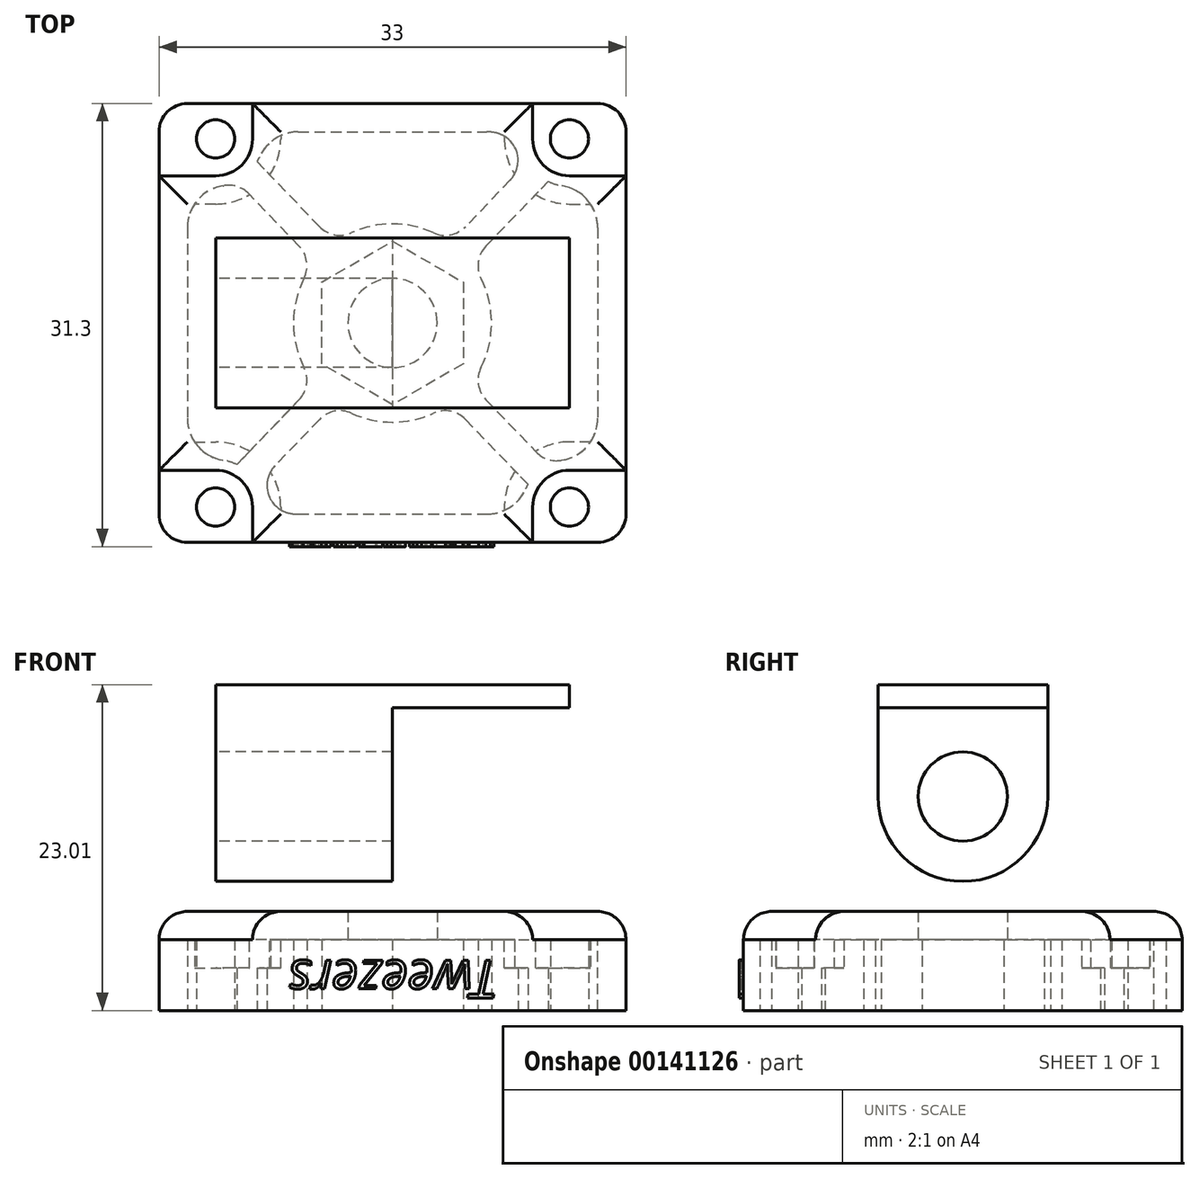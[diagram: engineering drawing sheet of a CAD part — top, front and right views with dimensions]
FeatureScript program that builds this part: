
annotation { "Feature Type Name" : "Feature", "Feature Type Description" : "" }
export const myFeature = defineFeature(function(context is Context, id is Id, definition is map)
    precondition{}
    {
        {
            var Q0;
            Q0=qCreatedBy(makeId("Top.planeOp"),FACE);
            var sketch = newSketch(context, id + "F0", { "sketchPlane" : qUnion([Q0])});
            skPoint(sketch, "E0", {"position": v(-12.5, 13) * mm});
            skPoint(sketch, "E1", {"position": v(12.5, 13) * mm});
            skPoint(sketch, "E2", {"position": v(-12.5, -13) * mm});
            skPoint(sketch, "E3", {"position": v(12.5, -13) * mm});
            skLineSegment(sketch, "E4", {"start": v(0, 33.85) * mm, "end": v(0, -36.04) * mm, "construction": true});
            skLineSegment(sketch, "E5", {"start": v(-33.7, 0) * mm, "end": v(36.4, 0) * mm, "construction": true});
            skLineSegment(sketch, "E6.bottom", {"start": v(-16.5, 15.5) * mm, "end": v(16.5, 15.5) * mm});
            skLineSegment(sketch, "E6.top", {"start": v(-16.5, -15.5) * mm, "end": v(16.5, -15.5) * mm});
            skLineSegment(sketch, "E6.left", {"start": v(-16.5, 15.5) * mm, "end": v(-16.5, -15.5) * mm});
            skLineSegment(sketch, "E6.right", {"start": v(16.5, 15.5) * mm, "end": v(16.5, -15.5) * mm});
            skCircle(sketch, "E7", {"center": v(-12.5, 13) * mm, "radius": 1.35 * mm});
            skCircle(sketch, "E8", {"center": v(12.5, 13) * mm, "radius": 1.35 * mm});
            skCircle(sketch, "E9", {"center": v(-12.5, -13) * mm, "radius": 1.35 * mm});
            skCircle(sketch, "E10", {"center": v(12.5, -13) * mm, "radius": 1.35 * mm});
            skSolve(sketch);
        }
        {
            var Q0;
            Q0=makeQuery(id+"F0.imprint","IMPRINT",FACE,{"disambiguationData":[TD([[makeQuery(id+"F0.imprint","IMPRINT",EDGE,{"derivedFrom":sQuery(id+"F0.wireOp",EDGE,"E6.bottom")}),-1.0]])]});
            extrude(context, id + "F1", {"entities" : qUnion([Q0]), "depth" : 7 * mm});
        }
        {
            var Q0;
            Q0=makeQuery(id+"F1.opExtrude","CAP_FACE",FACE,{"disambiguationData":[OSD([sQuery(id+"F0.wireOp",EDGE,"E6.bottom"),sQuery(id+"F0.wireOp",EDGE,"E6.top"),sQuery(id+"F0.wireOp",EDGE,"E6.left"),sQuery(id+"F0.wireOp",EDGE,"E6.right"),sQuery(id+"F0.wireOp",EDGE,"E7"),sQuery(id+"F0.wireOp",EDGE,"E8"),sQuery(id+"F0.wireOp",EDGE,"E9"),sQuery(id+"F0.wireOp",EDGE,"E10")])],"isStart":false});
            var sketch = newSketch(context, id + "F2", { "sketchPlane" : qUnion([Q0])});
            skLineSegment(sketch, "E11", {"start": v(9.9, 15.5) * mm, "end": v(9.9, 13) * mm});
            skLineSegment(sketch, "E12", {"start": v(12.5, 10.4) * mm, "end": v(16.5, 10.4) * mm});
            skPoint(sketch, "E13.visualSharp", {"position": v(9.9, 10.4) * mm});
            skArc(sketch, "E13.filletArc", {"start": v(9.9, 13) * mm, "mid": v(10.66, 11.16) * mm, "end": v(12.5, 10.4) * mm});
            skLineSegment(sketch, "E14", {"start": v(-9.9, 15.5) * mm, "end": v(-9.9, 13) * mm});
            skLineSegment(sketch, "E15", {"start": v(-12.5, 10.4) * mm, "end": v(-16.5, 10.4) * mm});
            skPoint(sketch, "E16.visualSharp", {"position": v(-9.9, 10.4) * mm});
            skArc(sketch, "E16.filletArc", {"start": v(-12.5, 10.4) * mm, "mid": v(-10.66, 11.16) * mm, "end": v(-9.9, 13) * mm});
            skLineSegment(sketch, "E17", {"start": v(-16.5, -10.4) * mm, "end": v(-12.5, -10.4) * mm});
            skLineSegment(sketch, "E18", {"start": v(-9.9, -13) * mm, "end": v(-9.9, -15.5) * mm});
            skPoint(sketch, "E19.visualSharp", {"position": v(-9.9, -10.4) * mm});
            skArc(sketch, "E19.filletArc", {"start": v(-9.9, -13) * mm, "mid": v(-10.66, -11.16) * mm, "end": v(-12.5, -10.4) * mm});
            skLineSegment(sketch, "E20", {"start": v(16.5, -10.4) * mm, "end": v(12.5, -10.4) * mm});
            skLineSegment(sketch, "E21", {"start": v(9.9, -13) * mm, "end": v(9.9, -15.5) * mm});
            skPoint(sketch, "E22.visualSharp", {"position": v(9.9, -10.4) * mm});
            skArc(sketch, "E22.filletArc", {"start": v(12.5, -10.4) * mm, "mid": v(10.66, -11.16) * mm, "end": v(9.9, -13) * mm});
            skSolve(sketch);
        }
        {
            var Q0;
            Q0=makeQuery(id+"F2.imprint","IMPRINT",FACE,{"disambiguationData":[TD([[makeQuery(id+"F2.imprint","IMPRINT",EDGE,{"derivedFrom":makeQuery(id+"F1.opExtrude","CAP_EDGE",EDGE,{"disambiguationData":[OSD([sQuery(id+"F0.wireOp",EDGE,"E7")])],"isStart":false})}),-1.0]])]});
            var Q1;
            Q1=makeQuery(id+"F2.imprint","IMPRINT",FACE,{"disambiguationData":[TD([[makeQuery(id+"F2.imprint","IMPRINT",EDGE,{"derivedFrom":makeQuery(id+"F1.opExtrude","CAP_EDGE",EDGE,{"disambiguationData":[OSD([sQuery(id+"F0.wireOp",EDGE,"E8")])],"isStart":false})}),-1.0]])]});
            var Q2;
            {var subQ4=sQuery(id+"F2.wireOp",EDGE,"E17");Q2=makeQuery(id+"F2.imprint","IMPRINT",FACE,{"disambiguationData":[TD([[makeQuery(id+"F2.imprint","IMPRINT",EDGE,{"derivedFrom":subQ4}),-1.0]])]});}
            var Q3;
            {var subQ1=sQuery(id+"F2.wireOp",EDGE,"E20");Q3=makeQuery(id+"F2.imprint","IMPRINT",FACE,{"disambiguationData":[TD([[makeQuery(id+"F2.imprint","IMPRINT",EDGE,{"derivedFrom":subQ1}),1.0]])]});}
            extrude(context, id + "F3", {"entities" : qUnion([Q0, Q1, Q2, Q3]), "operationType" : NewBodyOperationType.REMOVE, "oppositeDirection" : true, "depth" : 2 * mm});
        }
        {
            var Q0;
            Q0=makeQuery(id+"F1.opExtrude","CAP_FACE",FACE,{"disambiguationData":[OSD([sQuery(id+"F0.wireOp",EDGE,"E6.bottom"),sQuery(id+"F0.wireOp",EDGE,"E6.top"),sQuery(id+"F0.wireOp",EDGE,"E6.left"),sQuery(id+"F0.wireOp",EDGE,"E6.right"),sQuery(id+"F0.wireOp",EDGE,"E7"),sQuery(id+"F0.wireOp",EDGE,"E8"),sQuery(id+"F0.wireOp",EDGE,"E9"),sQuery(id+"F0.wireOp",EDGE,"E10")])],"isStart":true});
            shell(context, id + "F4", {"entities" : qUnion([Q0]), "thickness" : 2 * mm});
        }
        {
            var Q0;
            Q0=makeQuery(id+"F1.opExtrude","CAP_FACE",FACE,{"disambiguationData":[OSD([sQuery(id+"F0.wireOp",EDGE,"E6.bottom"),sQuery(id+"F0.wireOp",EDGE,"E6.top"),sQuery(id+"F0.wireOp",EDGE,"E6.left"),sQuery(id+"F0.wireOp",EDGE,"E6.right"),sQuery(id+"F0.wireOp",EDGE,"E7"),sQuery(id+"F0.wireOp",EDGE,"E8"),sQuery(id+"F0.wireOp",EDGE,"E9"),sQuery(id+"F0.wireOp",EDGE,"E10")])],"isStart":false});
            var Q1;
            Q1=makeQuery(id+"F3.boolean.opBoolean","COPY",EDGE,{"derivedFrom":makeQuery(id+"F3.opExtrude","SWEPT_EDGE",EDGE,{"disambiguationData":[OSD([sQuery(id+"F0.wireOp",EDGE,"E6.top"),sQuery(id+"F2.wireOp",EDGE,"E18")])]})});
            var Q2;
            Q2=makeQuery(id+"F3.boolean.opBoolean","COPY",EDGE,{"derivedFrom":makeQuery(id+"F3.opExtrude","SWEPT_EDGE",EDGE,{"disambiguationData":[OSD([sQuery(id+"F0.wireOp",EDGE,"E6.left"),sQuery(id+"F2.wireOp",EDGE,"E17")])]})});
            var Q3;
            Q3=makeQuery(id+"F1.opExtrude","SWEPT_EDGE",EDGE,{"disambiguationData":[OSD([sQuery(id+"F0.wireOp",EDGE,"E6.bottom"),sQuery(id+"F0.wireOp",EDGE,"E6.right")])]});
            var Q4;
            Q4=makeQuery(id+"F3.boolean.opBoolean","COPY",EDGE,{"derivedFrom":makeQuery(id+"F3.opExtrude","SWEPT_EDGE",EDGE,{"disambiguationData":[OSD([sQuery(id+"F0.wireOp",EDGE,"E6.bottom"),sQuery(id+"F2.wireOp",EDGE,"E11")])]})});
            var Q5;
            Q5=makeQuery(id+"F3.boolean.opBoolean","COPY",EDGE,{"derivedFrom":makeQuery(id+"F3.opExtrude","SWEPT_EDGE",EDGE,{"disambiguationData":[OSD([sQuery(id+"F0.wireOp",EDGE,"E6.right"),sQuery(id+"F2.wireOp",EDGE,"E12")])]})});
            var Q6;
            Q6=makeQuery(id+"F3.boolean.opBoolean","COPY",EDGE,{"derivedFrom":makeQuery(id+"F3.opExtrude","SWEPT_EDGE",EDGE,{"disambiguationData":[OSD([sQuery(id+"F0.wireOp",EDGE,"E6.right"),sQuery(id+"F2.wireOp",EDGE,"E20")])]})});
            var Q7;
            Q7=makeQuery(id+"F1.opExtrude","SWEPT_EDGE",EDGE,{"disambiguationData":[OSD([sQuery(id+"F0.wireOp",EDGE,"E6.top"),sQuery(id+"F0.wireOp",EDGE,"E6.right")])]});
            var Q8;
            Q8=makeQuery(id+"F3.boolean.opBoolean","COPY",EDGE,{"derivedFrom":makeQuery(id+"F3.opExtrude","SWEPT_EDGE",EDGE,{"disambiguationData":[OSD([sQuery(id+"F0.wireOp",EDGE,"E6.top"),sQuery(id+"F2.wireOp",EDGE,"E21")])]})});
            var Q9;
            Q9=makeQuery(id+"F1.opExtrude","SWEPT_EDGE",EDGE,{"disambiguationData":[OSD([sQuery(id+"F0.wireOp",EDGE,"E6.top"),sQuery(id+"F0.wireOp",EDGE,"E6.left")])]});
            var Q10;
            Q10=makeQuery(id+"F3.boolean.opBoolean","COPY",EDGE,{"derivedFrom":makeQuery(id+"F3.opExtrude","SWEPT_EDGE",EDGE,{"disambiguationData":[OSD([sQuery(id+"F0.wireOp",EDGE,"E6.left"),sQuery(id+"F2.wireOp",EDGE,"E15")])]})});
            var Q11;
            Q11=makeQuery(id+"F3.boolean.opBoolean","COPY",EDGE,{"derivedFrom":makeQuery(id+"F3.opExtrude","SWEPT_EDGE",EDGE,{"disambiguationData":[OSD([sQuery(id+"F0.wireOp",EDGE,"E6.bottom"),sQuery(id+"F2.wireOp",EDGE,"E14")])]})});
            var Q12;
            Q12=makeQuery(id+"F1.opExtrude","SWEPT_EDGE",EDGE,{"disambiguationData":[OSD([sQuery(id+"F0.wireOp",EDGE,"E6.bottom"),sQuery(id+"F0.wireOp",EDGE,"E6.left")])]});
            fillet(context, id + "F5", {"entities" : qUnion([Q0, Q1, Q2, Q3, Q4, Q5, Q6, Q7, Q8, Q9, Q10, Q11, Q12]), "radius" : 2 * mm, "tangentPropagation" : true, "allowEdgeOverflow" : false});
        }
        {
            var Q0;
            Q0=qCreatedBy(makeId("Top.planeOp"),FACE);
            var sketch = newSketch(context, id + "F6", { "sketchPlane" : qUnion([Q0])});
            skPoint(sketch, "E23", {"position": v(0, 0) * mm});
            skCircle(sketch, "E24", {"center": v(0, 0) * mm, "radius": 3.15 * mm});
            skCircle(sketch, "E25.cCircle", {"center": v(0, 0) * mm, "radius": 5 * mm, "construction": true});
            skLineSegment(sketch, "E25.0", {"start": v(5, 2.89) * mm, "end": v(5, -2.89) * mm});
            skLineSegment(sketch, "E25.1", {"start": v(5, -2.89) * mm, "end": v(0, -5.77) * mm});
            skLineSegment(sketch, "E25.2", {"start": v(0, -5.77) * mm, "end": v(-5, -2.89) * mm});
            skLineSegment(sketch, "E25.3", {"start": v(-5, -2.89) * mm, "end": v(-5, 2.89) * mm});
            skLineSegment(sketch, "E25.4", {"start": v(-5, 2.89) * mm, "end": v(0, 5.77) * mm});
            skLineSegment(sketch, "E25.5", {"start": v(0, 5.77) * mm, "end": v(5, 2.89) * mm});
            skPoint(sketch, "E25.0.midPoint", {"position": v(5, 0) * mm});
            skCircle(sketch, "E26", {"center": v(0, 0) * mm, "radius": 7 * mm});
            skLineSegment(sketch, "E27", {"start": v(-4.08, -5.69) * mm, "end": v(-9.56, -11.39) * mm});
            skLineSegment(sketch, "E28", {"start": v(-11, -10) * mm, "end": v(-5.52, -4.3) * mm});
            skLineSegment(sketch, "E29", {"start": v(-12.5, -13) * mm, "end": v(0, 0) * mm, "construction": true});
            skLineSegment(sketch, "E30", {"start": v(0, 0) * mm, "end": v(12.5, -13) * mm, "construction": true});
            skLineSegment(sketch, "E31", {"start": v(4.08, -5.69) * mm, "end": v(9.56, -11.39) * mm});
            skLineSegment(sketch, "E32", {"start": v(5.52, -4.3) * mm, "end": v(11, -10) * mm});
            skLineSegment(sketch, "E33", {"start": v(-4.08, 5.69) * mm, "end": v(-9.56, 11.39) * mm});
            skLineSegment(sketch, "E34", {"start": v(-5.52, 4.3) * mm, "end": v(-11, 10) * mm});
            skLineSegment(sketch, "E35", {"start": v(0, 0) * mm, "end": v(-12.5, 13) * mm, "construction": true});
            skLineSegment(sketch, "E36", {"start": v(12.5, 13) * mm, "end": v(0, 0) * mm, "construction": true});
            skArc(sketch, "E37.0", {"start": v(9.19, 13.5) * mm, "mid": v(10.78, 10.13) * mm, "end": v(14.5, 10.31) * mm});
            skLineSegment(sketch, "E38", {"start": v(5.52, 4.3) * mm, "end": v(11, 10) * mm});
            skLineSegment(sketch, "E39", {"start": v(9.56, 11.39) * mm, "end": v(4.08, 5.69) * mm});
            skArc(sketch, "E40.0", {"start": v(14.5, -10.31) * mm, "mid": v(10.78, -10.13) * mm, "end": v(9.19, -13.5) * mm});
            skArc(sketch, "E41.0", {"start": v(-9.19, -13.5) * mm, "mid": v(-10.78, -10.13) * mm, "end": v(-14.5, -10.31) * mm});
            skArc(sketch, "E42.0", {"start": v(-14.5, 10.31) * mm, "mid": v(-10.78, 10.13) * mm, "end": v(-9.19, 13.5) * mm});
            skSolve(sketch);
        }
        {
            var Q0;
            {var subQ0=sQuery(id+"F6.wireOp",EDGE,"E38");var subQ1=sQuery(id+"F6.wireOp",EDGE,"E26");var subQ2=makeQuery(id+"F6.imprint","INTERSECT",VERTEX,{"derivedFrom":[subQ1,subQ0]});Q0=makeQuery(id+"F6.imprint","IMPRINT",FACE,{"disambiguationData":[TD([[makeQuery(id+"F6.imprint","IMPRINT",EDGE,{"disambiguationData":[TD([[subQ2,-1.0]])],"derivedFrom":subQ1}),-1.0]])]});}
            var Q1;
            Q1=makeQuery(id+"F6.imprint","IMPRINT",FACE,{"disambiguationData":[TD([[makeQuery(id+"F6.imprint","IMPRINT",EDGE,{"derivedFrom":sQuery(id+"F6.wireOp",EDGE,"E25.0")}),1.0]])]});
            var Q2;
            {var subQ0=sQuery(id+"F6.wireOp",EDGE,"E27");Q2=makeQuery(id+"F6.imprint","IMPRINT",FACE,{"disambiguationData":[TD([[makeQuery(id+"F6.imprint","IMPRINT",EDGE,{"derivedFrom":subQ0}),-1.0]])]});}
            var Q3;
            {var subQ0=sQuery(id+"F6.wireOp",EDGE,"E33");Q3=makeQuery(id+"F6.imprint","IMPRINT",FACE,{"disambiguationData":[TD([[makeQuery(id+"F6.imprint","IMPRINT",EDGE,{"derivedFrom":subQ0}),1.0]])]});}
            var Q4;
            {var subQ0=sQuery(id+"F6.wireOp",EDGE,"E31");Q4=makeQuery(id+"F6.imprint","IMPRINT",FACE,{"disambiguationData":[TD([[makeQuery(id+"F6.imprint","IMPRINT",EDGE,{"derivedFrom":subQ0}),1.0]])]});}
            var Q5;
            Q5=makeQuery(id+"F4.opShell","OFFSET_FACE",FACE,{"disambiguationData":[OSD([sQuery(id+"F0.wireOp",EDGE,"E6.bottom"),sQuery(id+"F0.wireOp",EDGE,"E6.top"),sQuery(id+"F0.wireOp",EDGE,"E6.left"),sQuery(id+"F0.wireOp",EDGE,"E6.right"),sQuery(id+"F0.wireOp",EDGE,"E7"),sQuery(id+"F0.wireOp",EDGE,"E8"),sQuery(id+"F0.wireOp",EDGE,"E9"),sQuery(id+"F0.wireOp",EDGE,"E10")])]});
            extrude(context, id + "F7", {"entities" : qUnion([Q0, Q1, Q2, Q3, Q4]), "operationType" : NewBodyOperationType.ADD, "endBound" : BoundingType.UP_TO_SURFACE, "endBoundEntityFace" : qUnion([Q5]), "depth" : 25 * mm});
        }
        {
            var Q0;
            Q0=makeQuery(id+"F6.imprint","IMPRINT",FACE,{"disambiguationData":[TD([[makeQuery(id+"F6.imprint","IMPRINT",EDGE,{"derivedFrom":sQuery(id+"F6.wireOp",EDGE,"E24")}),1.0]])]});
            extrude(context, id + "F8", {"entities" : qUnion([Q0]), "operationType" : NewBodyOperationType.REMOVE, "endBound" : BoundingType.THROUGH_ALL, "depth" : 25 * mm});
        }
        {
            var Q0;
            Q0=makeQuery(id+"F4.opShell","TWEAK_EDGE",EDGE,{"derivedFrom":[makeQuery(id+"F1.opExtrude","SWEPT_FACE",FACE,{"disambiguationData":[OSD([sQuery(id+"F0.wireOp",EDGE,"E6.right")])]}),makeQuery(id+"F1.opExtrude","SWEPT_FACE",FACE,{"disambiguationData":[OSD([sQuery(id+"F0.wireOp",EDGE,"E10")])]})]});
            var Q1;
            Q1=makeQuery(id+"F4.opShell","TWEAK_EDGE",EDGE,{"derivedFrom":[makeQuery(id+"F1.opExtrude","SWEPT_FACE",FACE,{"disambiguationData":[OSD([sQuery(id+"F0.wireOp",EDGE,"E6.top")])]}),makeQuery(id+"F1.opExtrude","SWEPT_FACE",FACE,{"disambiguationData":[OSD([sQuery(id+"F0.wireOp",EDGE,"E10")])]})]});
            var Q2;
            Q2=makeQuery(id+"F4.opShell","TWEAK_EDGE",EDGE,{"derivedFrom":[makeQuery(id+"F1.opExtrude","SWEPT_FACE",FACE,{"disambiguationData":[OSD([sQuery(id+"F0.wireOp",EDGE,"E6.top")])]}),makeQuery(id+"F1.opExtrude","SWEPT_FACE",FACE,{"disambiguationData":[OSD([sQuery(id+"F0.wireOp",EDGE,"E9")])]})]});
            var Q3;
            Q3=makeQuery(id+"F4.opShell","TWEAK_EDGE",EDGE,{"derivedFrom":[makeQuery(id+"F1.opExtrude","SWEPT_FACE",FACE,{"disambiguationData":[OSD([sQuery(id+"F0.wireOp",EDGE,"E6.left")])]}),makeQuery(id+"F1.opExtrude","SWEPT_FACE",FACE,{"disambiguationData":[OSD([sQuery(id+"F0.wireOp",EDGE,"E9")])]})]});
            var Q4;
            Q4=makeQuery(id+"F4.opShell","TWEAK_EDGE",EDGE,{"derivedFrom":[makeQuery(id+"F1.opExtrude","SWEPT_FACE",FACE,{"disambiguationData":[OSD([sQuery(id+"F0.wireOp",EDGE,"E6.left")])]}),makeQuery(id+"F1.opExtrude","SWEPT_FACE",FACE,{"disambiguationData":[OSD([sQuery(id+"F0.wireOp",EDGE,"E7")])]})]});
            var Q5;
            Q5=makeQuery(id+"F4.opShell","TWEAK_EDGE",EDGE,{"derivedFrom":[makeQuery(id+"F1.opExtrude","SWEPT_FACE",FACE,{"disambiguationData":[OSD([sQuery(id+"F0.wireOp",EDGE,"E6.bottom")])]}),makeQuery(id+"F1.opExtrude","SWEPT_FACE",FACE,{"disambiguationData":[OSD([sQuery(id+"F0.wireOp",EDGE,"E7")])]})]});
            var Q6;
            Q6=makeQuery(id+"F4.opShell","TWEAK_EDGE",EDGE,{"derivedFrom":[makeQuery(id+"F1.opExtrude","SWEPT_FACE",FACE,{"disambiguationData":[OSD([sQuery(id+"F0.wireOp",EDGE,"E6.right")])]}),makeQuery(id+"F1.opExtrude","SWEPT_FACE",FACE,{"disambiguationData":[OSD([sQuery(id+"F0.wireOp",EDGE,"E8")])]})]});
            var Q7;
            Q7=makeQuery(id+"F4.opShell","TWEAK_EDGE",EDGE,{"derivedFrom":[makeQuery(id+"F1.opExtrude","SWEPT_FACE",FACE,{"disambiguationData":[OSD([sQuery(id+"F0.wireOp",EDGE,"E6.bottom")])]}),makeQuery(id+"F1.opExtrude","SWEPT_FACE",FACE,{"disambiguationData":[OSD([sQuery(id+"F0.wireOp",EDGE,"E8")])]})]});
            fillet(context, id + "F9", {"entities" : qUnion([Q0, Q1, Q2, Q3, Q4, Q5, Q6, Q7]), "radius" : 3 * mm, "allowEdgeOverflow" : false});
        }
        {
            var Q0;
            Q0=makeQuery(id+"F1.opExtrude","SWEPT_FACE",FACE,{"disambiguationData":[OSD([sQuery(id+"F0.wireOp",EDGE,"E6.top")])]});
            var sketch = newSketch(context, id + "F10", { "sketchPlane" : qUnion([Q0])});
            skText(sketch, "E43", { "text": "Tweezers", "fontName": "OpenSans-Italic.ttf"});
            const initialGuessF10  = {"E43": [0.0075, 0.00355, -1, 0, 0.0027]};
            skSetInitialGuess(sketch, initialGuessF10);
            skSolve(sketch);
        }
        {
            var Q0;
            Q0=qSketchRegion(id+"F10",true);
            extrude(context, id + "F11", {"entities" : qUnion([Q0]), "operationType" : NewBodyOperationType.ADD, "depth" : 0.3 * mm});
        }
        {
            var Q0;
            Q0=makeQuery(id+"F7.opExtrude","SWEPT_EDGE",EDGE,{"disambiguationData":[OSD([sQuery(id+"F6.wireOp",EDGE,"E26"),sQuery(id+"F6.wireOp",EDGE,"E28")])]});
            var Q1;
            Q1=makeQuery(id+"F7.opExtrude","SWEPT_EDGE",EDGE,{"disambiguationData":[OSD([sQuery(id+"F6.wireOp",EDGE,"E26"),sQuery(id+"F6.wireOp",EDGE,"E34")])]});
            var Q2;
            Q2=makeQuery(id+"F7.opExtrude","SWEPT_EDGE",EDGE,{"disambiguationData":[OSD([sQuery(id+"F6.wireOp",EDGE,"E26"),sQuery(id+"F6.wireOp",EDGE,"E33")])]});
            var Q3;
            Q3=makeQuery(id+"F7.opExtrude","SWEPT_EDGE",EDGE,{"disambiguationData":[OSD([sQuery(id+"F6.wireOp",EDGE,"E26"),sQuery(id+"F6.wireOp",EDGE,"E39")])]});
            var Q4;
            Q4=makeQuery(id+"F7.opExtrude","SWEPT_EDGE",EDGE,{"disambiguationData":[OSD([sQuery(id+"F6.wireOp",EDGE,"E26"),sQuery(id+"F6.wireOp",EDGE,"E38")])]});
            var Q5;
            Q5=makeQuery(id+"F7.opExtrude","SWEPT_EDGE",EDGE,{"disambiguationData":[OSD([sQuery(id+"F6.wireOp",EDGE,"E26"),sQuery(id+"F6.wireOp",EDGE,"E32")])]});
            var Q6;
            Q6=makeQuery(id+"F7.opExtrude","SWEPT_EDGE",EDGE,{"disambiguationData":[OSD([sQuery(id+"F6.wireOp",EDGE,"E26"),sQuery(id+"F6.wireOp",EDGE,"E31")])]});
            var Q7;
            Q7=makeQuery(id+"F7.opExtrude","SWEPT_EDGE",EDGE,{"disambiguationData":[OSD([sQuery(id+"F6.wireOp",EDGE,"E26"),sQuery(id+"F6.wireOp",EDGE,"E27")])]});
            var Q8;
            Q8=makeQuery(id+"F7.opExtrude","SWEPT_EDGE",EDGE,{"disambiguationData":[OSD([sQuery(id+"F6.wireOp",EDGE,"E33"),sQuery(id+"F6.wireOp",EDGE,"E42.0")])]});
            var Q9;
            Q9=makeQuery(id+"F7.opExtrude","SWEPT_EDGE",EDGE,{"disambiguationData":[OSD([sQuery(id+"F6.wireOp",EDGE,"E34"),sQuery(id+"F6.wireOp",EDGE,"E42.0")])]});
            var Q10;
            Q10=makeQuery(id+"F7.opExtrude","SWEPT_EDGE",EDGE,{"disambiguationData":[OSD([sQuery(id+"F6.wireOp",EDGE,"E37.0"),sQuery(id+"F6.wireOp",EDGE,"E38")])]});
            var Q11;
            Q11=makeQuery(id+"F7.opExtrude","SWEPT_EDGE",EDGE,{"disambiguationData":[OSD([sQuery(id+"F6.wireOp",EDGE,"E37.0"),sQuery(id+"F6.wireOp",EDGE,"E39")])]});
            var Q12;
            Q12=makeQuery(id+"F7.opExtrude","SWEPT_EDGE",EDGE,{"disambiguationData":[OSD([sQuery(id+"F6.wireOp",EDGE,"E32"),sQuery(id+"F6.wireOp",EDGE,"E40.0")])]});
            var Q13;
            Q13=makeQuery(id+"F7.opExtrude","SWEPT_EDGE",EDGE,{"disambiguationData":[OSD([sQuery(id+"F6.wireOp",EDGE,"E31"),sQuery(id+"F6.wireOp",EDGE,"E40.0")])]});
            var Q14;
            Q14=makeQuery(id+"F7.opExtrude","SWEPT_EDGE",EDGE,{"disambiguationData":[OSD([sQuery(id+"F6.wireOp",EDGE,"E28"),sQuery(id+"F6.wireOp",EDGE,"E41.0")])]});
            var Q15;
            Q15=makeQuery(id+"F7.opExtrude","SWEPT_EDGE",EDGE,{"disambiguationData":[OSD([sQuery(id+"F6.wireOp",EDGE,"E27"),sQuery(id+"F6.wireOp",EDGE,"E41.0")])]});
            fillet(context, id + "F12", {"entities" : qUnion([Q0, Q1, Q2, Q3, Q4, Q5, Q6, Q7, Q8, Q9, Q10, Q11, Q12, Q13, Q14, Q15]), "radius" : 2 * mm, "allowEdgeOverflow" : false});
        }
        {
            var Q0;
            Q0=qCreatedBy(makeId("Right.planeOp"),FACE);
            var sketch = newSketch(context, id + "F13", { "sketchPlane" : qUnion([Q0])});
            skCircle(sketch, "E44", {"center": v(0, 15.12) * mm, "radius": 6 * mm});
            skCircle(sketch, "E45", {"center": v(0, 15.12) * mm, "radius": 3.15 * mm});
            skLineSegment(sketch, "E46.bottom", {"start": v(-6, 23.01) * mm, "end": v(6, 23.01) * mm});
            skLineSegment(sketch, "E46.top", {"start": v(-6, 7) * mm, "end": v(6, 7) * mm});
            skLineSegment(sketch, "E46.left", {"start": v(-6, 23.01) * mm, "end": v(-6, 15.12) * mm});
            skLineSegment(sketch, "E46.right", {"start": v(6, 23.01) * mm, "end": v(6, 15.12) * mm});
            skLineSegment(sketch, "E47.0", {"start": v(3.15, 7) * mm, "end": v(-3.15, 7) * mm});
            skLineSegment(sketch, "E48", {"start": v(6, 15.12) * mm, "end": v(6, 7) * mm});
            skLineSegment(sketch, "E49", {"start": v(-6, 15.12) * mm, "end": v(-6, 7) * mm});
            skLineSegment(sketch, "E50", {"start": v(-6, 15.12) * mm, "end": v(6, 15.12) * mm});
            skSolve(sketch);
        }
        {
            var Q0;
            {var subQ0=sQuery(id+"F13.wireOp",EDGE,"E50");var subQ4=sQuery(id+"F13.wireOp",EDGE,"E45");var subQ5=makeQuery(id+"F13.imprint","INTERSECT",VERTEX,{"disambiguationData":[OD(0.0)],"derivedFrom":[subQ4,subQ0]});Q0=makeQuery(id+"F13.imprint","IMPRINT",FACE,{"disambiguationData":[TD([[makeQuery(id+"F13.imprint","IMPRINT",EDGE,{"disambiguationData":[TD([[subQ5,-1.0]])],"derivedFrom":subQ4}),-1.0]])]});}
            var Q1;
            {var subQ0=sQuery(id+"F13.wireOp",EDGE,"E50");var subQ4=sQuery(id+"F13.wireOp",EDGE,"E45");var subQ5=makeQuery(id+"F13.imprint","INTERSECT",VERTEX,{"disambiguationData":[OD(0.0)],"derivedFrom":[subQ4,subQ0]});Q1=makeQuery(id+"F13.imprint","IMPRINT",FACE,{"disambiguationData":[TD([[makeQuery(id+"F13.imprint","IMPRINT",EDGE,{"disambiguationData":[TD([[subQ5,1.0]])],"derivedFrom":subQ4}),-1.0]])]});}
            var Q2;
            Q2=makeQuery(id+"F13.imprint","IMPRINT",FACE,{"disambiguationData":[TD([[makeQuery(id+"F13.imprint","IMPRINT",EDGE,{"derivedFrom":sQuery(id+"F13.wireOp",EDGE,"E46.bottom")}),-1.0]])]});
            extrude(context, id + "F14", {"entities" : qUnion([Q0, Q1, Q2]), "endBound" : BoundingType.SYMMETRIC, "depth" : 25 * mm});
        }
        {
            var Q0;
            {var subQ0=sQuery(id+"F13.wireOp",EDGE,"E47.0");Q0=makeQuery(id+"F13.imprint","IMPRINT",FACE,{"disambiguationData":[TD([[makeQuery(id+"F13.imprint","IMPRINT",EDGE,{"derivedFrom":subQ0}),-1.0]])]});}
            var Q1;
            {var subQ0=sQuery(id+"F13.wireOp",EDGE,"E50");var subQ4=sQuery(id+"F13.wireOp",EDGE,"E45");var subQ5=makeQuery(id+"F13.imprint","INTERSECT",VERTEX,{"disambiguationData":[OD(0.0)],"derivedFrom":[subQ4,subQ0]});Q1=makeQuery(id+"F13.imprint","IMPRINT",FACE,{"disambiguationData":[TD([[makeQuery(id+"F13.imprint","IMPRINT",EDGE,{"disambiguationData":[TD([[subQ5,-1.0]])],"derivedFrom":subQ4}),-1.0]])]});}
            var Q2;
            {var subQ0=sQuery(id+"F13.wireOp",EDGE,"E50");var subQ4=sQuery(id+"F13.wireOp",EDGE,"E45");var subQ5=makeQuery(id+"F13.imprint","INTERSECT",VERTEX,{"disambiguationData":[OD(0.0)],"derivedFrom":[subQ4,subQ0]});Q2=makeQuery(id+"F13.imprint","IMPRINT",FACE,{"disambiguationData":[TD([[makeQuery(id+"F13.imprint","IMPRINT",EDGE,{"disambiguationData":[TD([[subQ5,1.0]])],"derivedFrom":subQ4}),-1.0]])]});}
            extrude(context, id + "F15", {"entities" : qUnion([Q0, Q1, Q2]), "operationType" : NewBodyOperationType.ADD, "endBound" : BoundingType.SYMMETRIC, "depth" : 25 * mm});
        }
        {
            var Q0;
            Q0=qCreatedBy(makeId("Front.planeOp"),FACE);
            var sketch = newSketch(context, id + "F16", { "sketchPlane" : qUnion([Q0])});
            skLineSegment(sketch, "E51.bottom", {"start": v(9.24, 21.4) * mm, "end": v(8.96, 21.4) * mm});
            skLineSegment(sketch, "E51.top", {"start": v(9.24, 8.57) * mm, "end": v(8.96, 8.57) * mm});
            skLineSegment(sketch, "E51.left", {"start": v(8.96, 21.4) * mm, "end": v(8.96, 8.57) * mm});
            skLineSegment(sketch, "E51.right", {"start": v(9.24, 21.4) * mm, "end": v(9.24, 8.57) * mm});
            skLineSegment(sketch, "E52.bottom", {"start": v(8.96, 21.4) * mm, "end": v(5.37, 21.4) * mm});
            skLineSegment(sketch, "E52.top", {"start": v(8.96, 8.57) * mm, "end": v(5.37, 8.57) * mm});
            skLineSegment(sketch, "E52.right", {"start": v(5.37, 21.4) * mm, "end": v(5.37, 8.57) * mm});
            skLineSegment(sketch, "E53.bottom", {"start": v(9.24, 21.4) * mm, "end": v(12.8, 21.4) * mm});
            skLineSegment(sketch, "E53.top", {"start": v(9.24, 8.57) * mm, "end": v(12.8, 8.57) * mm});
            skLineSegment(sketch, "E53.right", {"start": v(12.8, 21.4) * mm, "end": v(12.8, 8.57) * mm});
            skLineSegment(sketch, "E54.bottom", {"start": v(5.37, 21.4) * mm, "end": v(4.8, 21.4) * mm});
            skLineSegment(sketch, "E54.top", {"start": v(5.37, 8.57) * mm, "end": v(4.8, 8.57) * mm});
            skLineSegment(sketch, "E54.right", {"start": v(4.8, 21.4) * mm, "end": v(4.8, 8.57) * mm});
            skLineSegment(sketch, "E55.bottom", {"start": v(4.8, 21.4) * mm, "end": v(0, 21.4) * mm});
            skLineSegment(sketch, "E55.top", {"start": v(4.8, 8.57) * mm, "end": v(0, 8.57) * mm});
            skLineSegment(sketch, "E55.right", {"start": v(0, 21.4) * mm, "end": v(0, 8.57) * mm});
            skSolve(sketch);
        }
        {
            var Q0;
            Q0=makeQuery(id+"F16.imprint","IMPRINT",FACE,{"disambiguationData":[TD([[makeQuery(id+"F16.imprint","IMPRINT",EDGE,{"derivedFrom":sQuery(id+"F16.wireOp",EDGE,"E53.bottom")}),-1.0]])]});
            var Q1;
            Q1=makeQuery(id+"F16.imprint","IMPRINT",FACE,{"disambiguationData":[TD([[makeQuery(id+"F16.imprint","IMPRINT",EDGE,{"derivedFrom":sQuery(id+"F16.wireOp",EDGE,"E55.bottom")}),1.0]])]});
            var Q2;
            Q2=makeQuery(id+"F16.imprint","IMPRINT",FACE,{"disambiguationData":[TD([[makeQuery(id+"F16.imprint","IMPRINT",EDGE,{"derivedFrom":sQuery(id+"F16.wireOp",EDGE,"E51.bottom")}),1.0]])]});
            var Q3;
            Q3=makeQuery(id+"F16.imprint","IMPRINT",FACE,{"disambiguationData":[TD([[makeQuery(id+"F16.imprint","IMPRINT",EDGE,{"derivedFrom":sQuery(id+"F16.wireOp",EDGE,"E54.bottom")}),1.0]])]});
            extrude(context, id + "F17", {"entities" : qUnion([Q0, Q1, Q2, Q3]), "operationType" : NewBodyOperationType.REMOVE, "endBound" : BoundingType.SYMMETRIC, "oppositeDirection" : true, "depth" : 25 * mm});
        }
        {
            var Q0;
            Q0=makeQuery(id+"F16.imprint","IMPRINT",FACE,{"disambiguationData":[TD([[makeQuery(id+"F16.imprint","IMPRINT",EDGE,{"derivedFrom":sQuery(id+"F16.wireOp",EDGE,"E52.bottom")}),1.0]])]});
            extrude(context, id + "F18", {"entities" : qUnion([Q0]), "operationType" : NewBodyOperationType.REMOVE, "endBound" : BoundingType.SYMMETRIC, "depth" : 25 * mm});
        }
    });
